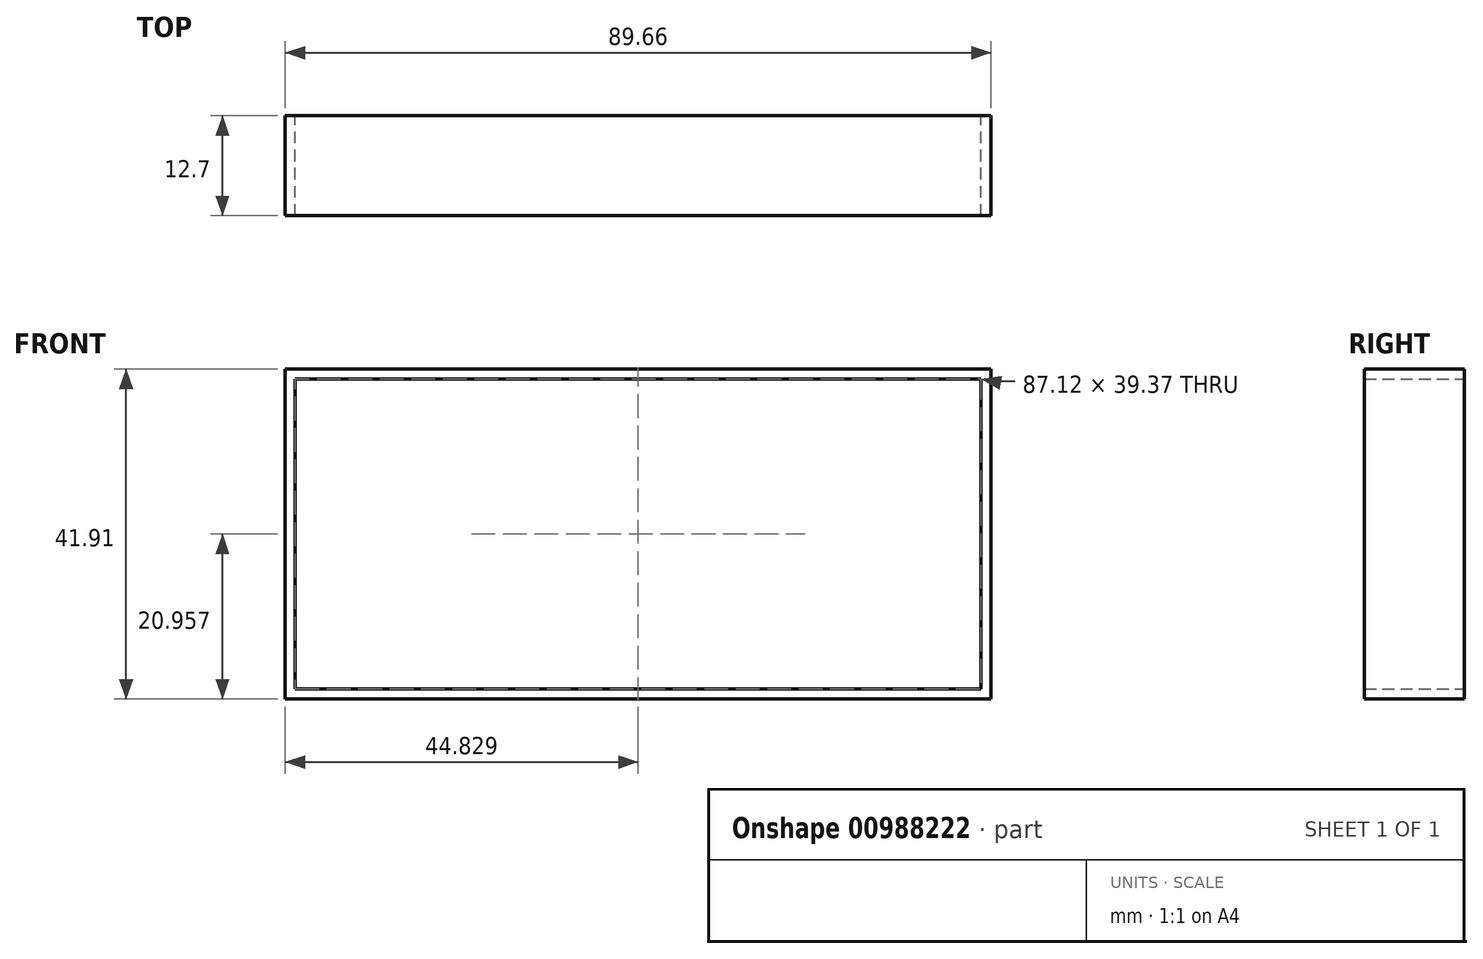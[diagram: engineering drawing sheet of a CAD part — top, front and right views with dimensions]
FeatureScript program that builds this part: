
annotation { "Feature Type Name" : "Feature", "Feature Type Description" : "" }
export const myFeature = defineFeature(function(context is Context, id is Id, definition is map)
    precondition{}
    {
        {
            var Q0;
            Q0=qCreatedBy(makeId("Front.planeOp"),FACE);
            var sketch = newSketch(context, id + "F0", { "sketchPlane" : qUnion([Q0])});
            skLineSegment(sketch, "E0.bottom", {"start": v(-41.4, 19.65) * mm, "end": v(45.72, 19.65) * mm});
            skLineSegment(sketch, "E0.top", {"start": v(-41.4, -19.72) * mm, "end": v(45.72, -19.72) * mm});
            skLineSegment(sketch, "E0.left", {"start": v(-41.4, 19.65) * mm, "end": v(-41.4, -19.72) * mm});
            skLineSegment(sketch, "E0.right", {"start": v(45.72, 19.65) * mm, "end": v(45.72, -19.72) * mm});
            skLineSegment(sketch, "E1.bottom", {"start": v(-42.67, 20.92) * mm, "end": v(47, 20.92) * mm});
            skLineSegment(sketch, "E1.top", {"start": v(-42.67, -20.99) * mm, "end": v(47, -20.99) * mm});
            skLineSegment(sketch, "E1.left", {"start": v(-42.67, 20.92) * mm, "end": v(-42.67, -20.99) * mm});
            skLineSegment(sketch, "E1.right", {"start": v(47, 20.92) * mm, "end": v(47, -20.99) * mm});
            skSolve(sketch);
        }
        {
            var Q0;
            Q0=makeQuery(id+"F0.imprint","IMPRINT",FACE,{"disambiguationData":[TD([[makeQuery(id+"F0.imprint","IMPRINT",EDGE,{"derivedFrom":sQuery(id+"F0.wireOp",EDGE,"E0.bottom")}),1.0]])]});
            extrude(context, id + "F1", {"entities" : qUnion([Q0]), "depth" : 12.7 * mm, "offsetDistance" : 25.4 * mm});
        }
    });
